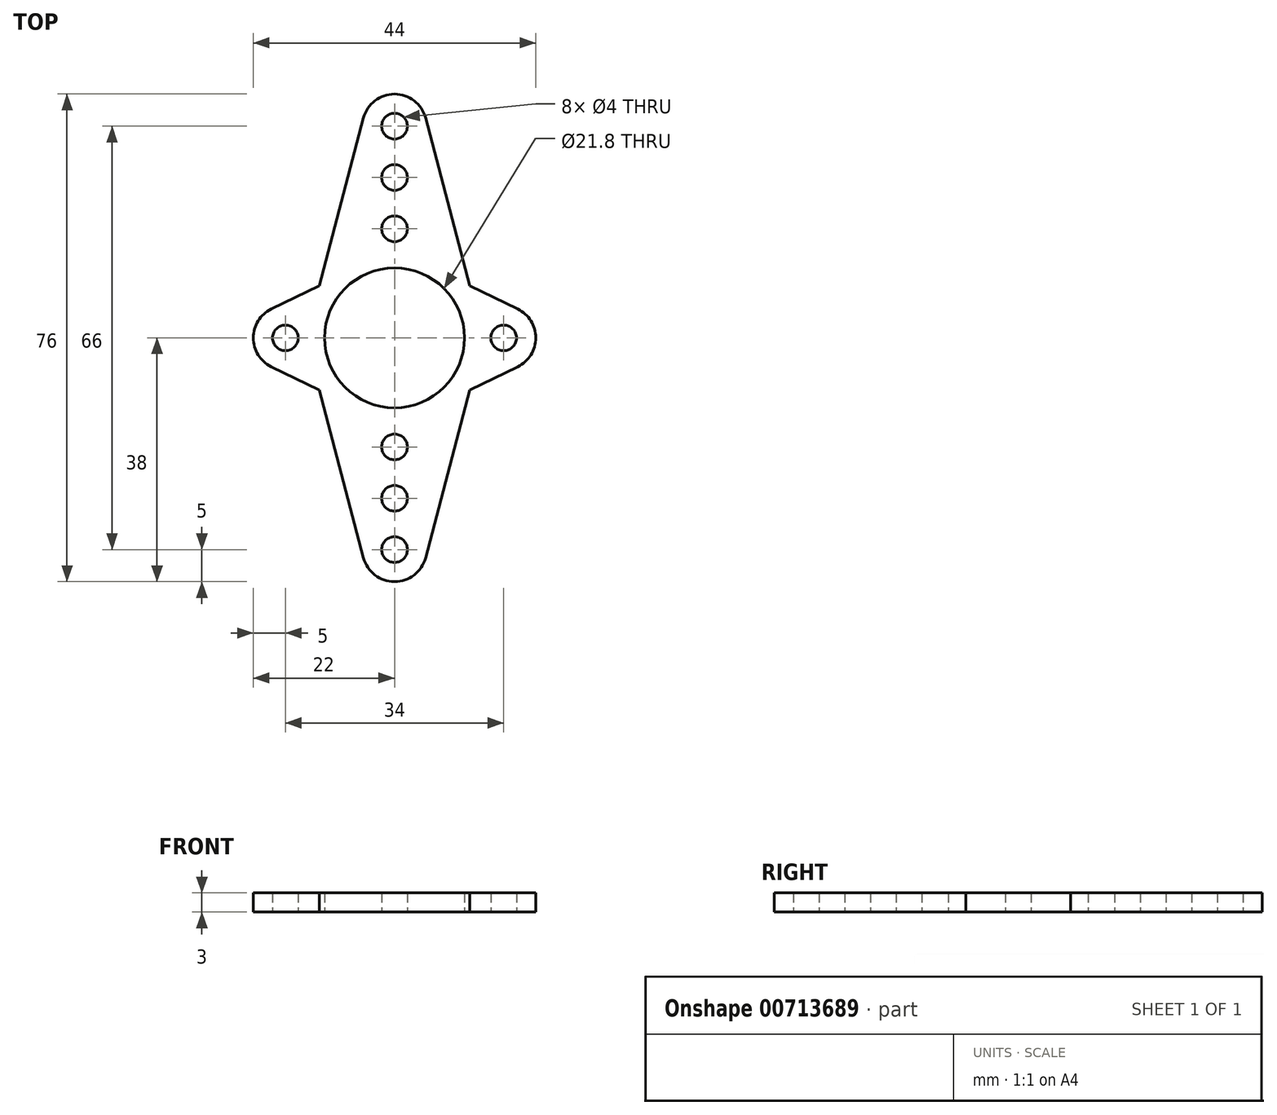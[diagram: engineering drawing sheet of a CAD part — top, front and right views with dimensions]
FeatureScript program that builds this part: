
annotation { "Feature Type Name" : "Feature", "Feature Type Description" : "" }
export const myFeature = defineFeature(function(context is Context, id is Id, definition is map)
    precondition{}
    {
        {
            var Q0;
            Q0=qCreatedBy(makeId("Top.planeOp"),FACE);
            var sketch = newSketch(context, id + "F0", { "sketchPlane" : qUnion([Q0])});
            skCircle(sketch, "E0", {"center": v(0, 0) * mm, "radius": 10.9 * mm});
            skCircle(sketch, "E1", {"center": v(0, 17) * mm, "radius": 2 * mm});
            skCircle(sketch, "E2", {"center": v(0, 25) * mm, "radius": 2 * mm});
            skCircle(sketch, "E3", {"center": v(0, 33) * mm, "radius": 2 * mm});
            skLineSegment(sketch, "E4", {"start": v(-11.75, 8.14) * mm, "end": v(-4.83, 34.28) * mm});
            skArc(sketch, "E5", {"start": v(-4.83, 34.28) * mm, "mid": v(-3.05, 36.96) * mm, "end": v(0, 38) * mm});
            skLineSegment(sketch, "E6", {"start": v(0, 0) * mm, "end": v(0, 44.04) * mm, "construction": true});
            skLineSegment(sketch, "E7", {"start": v(0, 0) * mm, "end": v(-24.44, 0) * mm, "construction": true});
            skLineSegment(sketch, "E8.MirrorCS", {"start": v(11.75, 8.14) * mm, "end": v(4.83, 34.28) * mm});
            skArc(sketch, "E9.MirrorCS", {"start": v(4.83, 34.28) * mm, "mid": v(3.05, 36.96) * mm, "end": v(0, 38) * mm});
            skLineSegment(sketch, "E10.MirrorCS", {"start": v(-11.75, -8.14) * mm, "end": v(-4.83, -34.28) * mm});
            skArc(sketch, "E11.MirrorCS", {"start": v(-4.83, -34.28) * mm, "mid": v(-3.05, -36.96) * mm, "end": v(0, -38) * mm});
            skArc(sketch, "E12.MirrorCS", {"start": v(4.83, -34.28) * mm, "mid": v(3.05, -36.96) * mm, "end": v(0, -38) * mm});
            skLineSegment(sketch, "E13.MirrorCS", {"start": v(11.75, -8.14) * mm, "end": v(4.83, -34.28) * mm});
            skCircle(sketch, "E14.MirrorC", {"center": v(0, -17) * mm, "radius": 2 * mm});
            skCircle(sketch, "E15.MirrorC", {"center": v(0, -25) * mm, "radius": 2 * mm});
            skCircle(sketch, "E16.MirrorC", {"center": v(0, -33) * mm, "radius": 2 * mm});
            skPoint(sketch, "E17.visualSharp", {"position": v(-13.9, 0) * mm});
            skPoint(sketch, "E18.visualSharp", {"position": v(13.9, 0) * mm});
            skCircle(sketch, "E19", {"center": v(17, 0) * mm, "radius": 2 * mm});
            skLineSegment(sketch, "E20", {"start": v(11.75, 8.14) * mm, "end": v(19.2, 4.49) * mm});
            skArc(sketch, "E21", {"start": v(19.2, 4.49) * mm, "mid": v(21.24, 2.65) * mm, "end": v(22, 0) * mm});
            skLineSegment(sketch, "E22.MirrorCS", {"start": v(11.75, -8.14) * mm, "end": v(19.2, -4.49) * mm});
            skArc(sketch, "E23.MirrorCS", {"start": v(19.2, -4.49) * mm, "mid": v(21.24, -2.65) * mm, "end": v(22, 0) * mm});
            skLineSegment(sketch, "E24.MirrorCS", {"start": v(-11.75, 8.14) * mm, "end": v(-19.2, 4.49) * mm});
            skArc(sketch, "E25.MirrorCS", {"start": v(-19.2, 4.49) * mm, "mid": v(-21.24, 2.65) * mm, "end": v(-22, 0) * mm});
            skArc(sketch, "E26.MirrorCS", {"start": v(-19.2, -4.49) * mm, "mid": v(-21.24, -2.65) * mm, "end": v(-22, 0) * mm});
            skLineSegment(sketch, "E27.MirrorCS", {"start": v(-11.75, -8.14) * mm, "end": v(-19.2, -4.49) * mm});
            skCircle(sketch, "E28.MirrorC", {"center": v(-17, 0) * mm, "radius": 2 * mm});
            skPoint(sketch, "E29.orphan", {"position": v(0, -13.9) * mm});
            skPoint(sketch, "E30.orphan", {"position": v(0, 13.9) * mm});
            skSolve(sketch);
        }
        {
            var Q0;
            Q0 = qSketchRegion(id + "F0", true);
            extrude(context, id + "F1", {"entities" : qUnion([Q0]), "depth" : 3 * mm, "offsetDistance" : 25 * mm});
        }
    });
